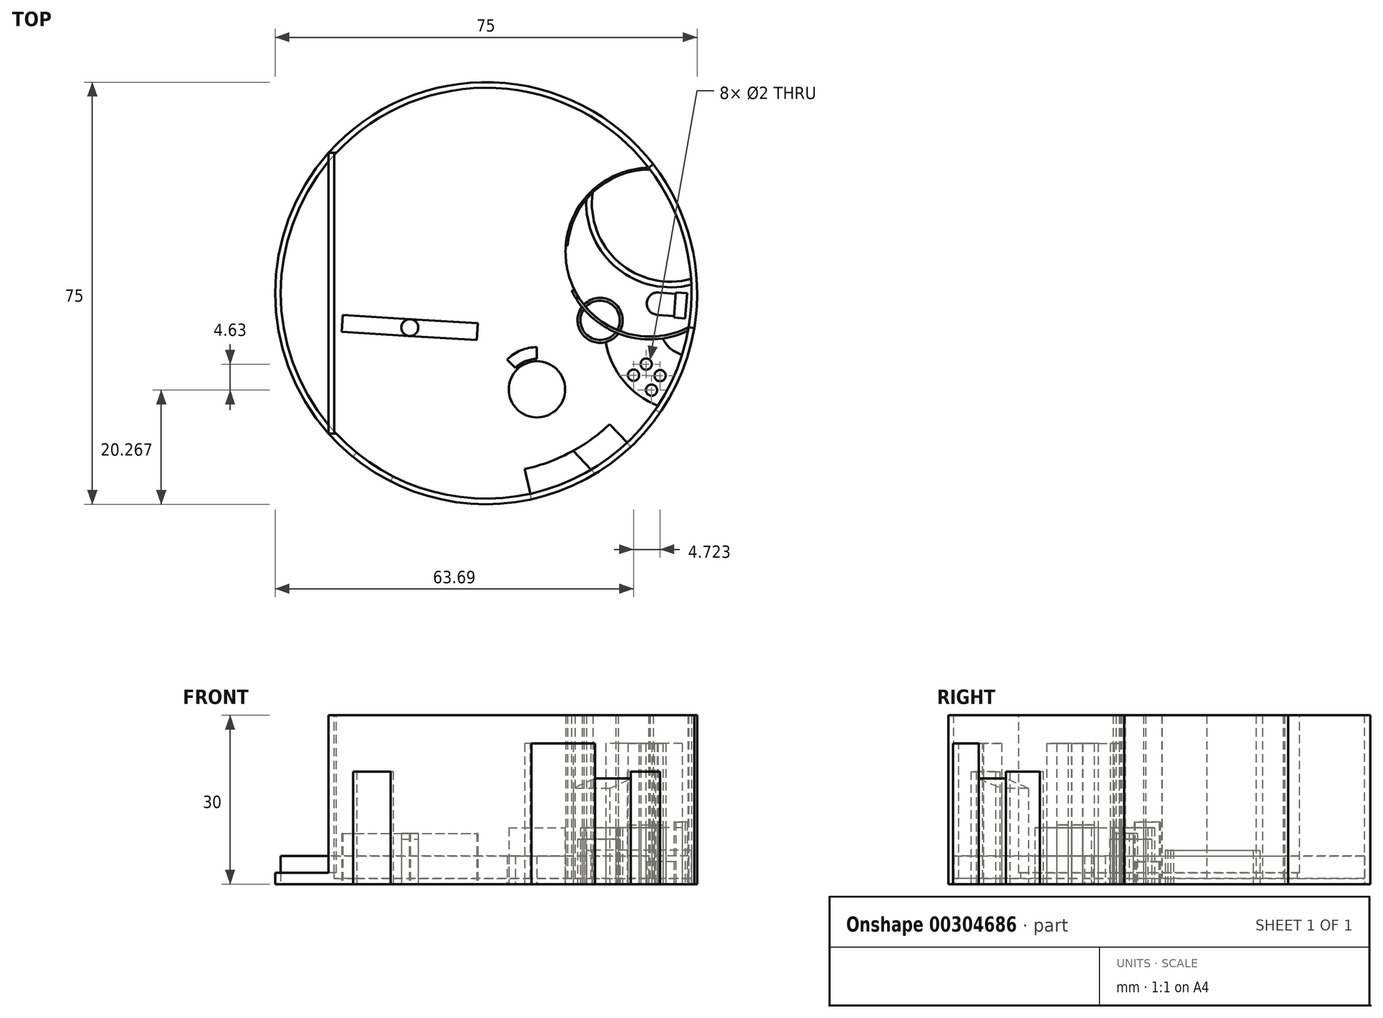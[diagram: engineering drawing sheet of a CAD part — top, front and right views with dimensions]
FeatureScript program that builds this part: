
annotation { "Feature Type Name" : "Feature", "Feature Type Description" : "" }
export const myFeature = defineFeature(function(context is Context, id is Id, definition is map)
    precondition{}
    {
        {
            var Q0;
            Q0=qCreatedBy(makeId("Top.planeOp"),FACE);
            var sketch = newSketch(context, id + "F0", { "sketchPlane" : qUnion([Q0])});
            skCircle(sketch, "E0", {"center": v(0, 0) * mm, "radius": 37.5 * mm});
            skSolve(sketch);
        }
        {
            var Q0;
            Q0=makeQuery(id+"F0.imprint","IMPRINT",FACE,{"disambiguationData":[TD([[makeQuery(id+"F0.imprint","IMPRINT",EDGE,{"derivedFrom":sQuery(id+"F0.wireOp",EDGE,"E0")}),1.0]])]});
            extrude(context, id + "F1", {"entities" : qUnion([Q0]), "oppositeDirection" : true, "depth" : 30 * mm});
        }
        {
            var Q0;
            Q0=qSketchRegion(id+"F0",true);
            var sketch = newSketch(context, id + "F2", { "sketchPlane" : qUnion([Q0])});
            skLineSegment(sketch, "E1", {"start": v(-28, 24.94) * mm, "end": v(-28, -24.94) * mm});
            skSolve(sketch);
        }
        {
            var Q0;
            {var subQ0=sQuery(id+"F2.wireOp",EDGE,"E1");Q0=makeQuery(id+"F2.imprint","IMPRINT",FACE,{"disambiguationData":[TD([[makeQuery(id+"F2.imprint","IMPRINT",EDGE,{"derivedFrom":subQ0}),-1.0]])]});}
            extrude(context, id + "F3", {"entities" : qUnion([Q0]), "operationType" : NewBodyOperationType.REMOVE, "oppositeDirection" : true, "depth" : 28 * mm});
        }
        {
            var Q0;
            {var subQ0=sQuery(id+"F2.wireOp",EDGE,"E1");Q0=makeQuery(id+"F2.imprint","IMPRINT",FACE,{"disambiguationData":[TD([[makeQuery(id+"F2.imprint","IMPRINT",EDGE,{"derivedFrom":subQ0}),1.0]])]});}
            var sketch = newSketch(context, id + "F4", { "sketchPlane" : qUnion([Q0])});
            skCircle(sketch, "E2", {"center": v(0, 0) * mm, "radius": 27 * mm});
            skArc(sketch, "E3", {"start": v(-28, 22.79) * mm, "mid": v(36.1, 0) * mm, "end": v(-28, -22.79) * mm});
            skLineSegment(sketch, "E4", {"start": v(-28, -22.79) * mm, "end": v(-28, 22.79) * mm});
            skSolve(sketch);
        }
        {
            var Q0;
            {var subQ0=sQuery(id+"F2.wireOp",EDGE,"E1");Q0=makeQuery(id+"F2.imprint","IMPRINT",FACE,{"disambiguationData":[TD([[makeQuery(id+"F2.imprint","IMPRINT",EDGE,{"derivedFrom":subQ0}),1.0]])]});}
            var sketch = newSketch(context, id + "F5", { "sketchPlane" : qUnion([Q0])});
            skArc(sketch, "E5", {"start": v(-23.66, -29.1) * mm, "mid": v(-20.43, -31.45) * mm, "end": v(-16.95, -33.45) * mm});
            skSolve(sketch);
        }
        {
            var Q0;
            Q0=makeQuery(id+"F1.opExtrude","CAP_FACE",FACE,{"disambiguationData":[OSD([sQuery(id+"F0.wireOp",EDGE,"E0")])],"isStart":false});
            var sketch = newSketch(context, id + "F6", { "sketchPlane" : qUnion([Q0])});
            skArc(sketch, "E6", {"start": v(-23.66, 29.1) * mm, "mid": v(-20.43, 31.45) * mm, "end": v(-16.95, 33.45) * mm});
            skArc(sketch, "E7", {"start": v(-23.03, 28.32) * mm, "mid": v(-19.88, 30.61) * mm, "end": v(-16.5, 32.56) * mm});
            skLineSegment(sketch, "E8", {"start": v(-23.66, 29.1) * mm, "end": v(-23.03, 28.32) * mm});
            skLineSegment(sketch, "E9", {"start": v(-16.95, 33.45) * mm, "end": v(-16.5, 32.56) * mm});
            skLineSegment(sketch, "E10", {"start": v(0, 0) * mm, "end": v(-23.66, 29.1) * mm, "construction": true});
            skLineSegment(sketch, "E11", {"start": v(-16.95, 33.45) * mm, "end": v(0, 0) * mm, "construction": true});
            skSolve(sketch);
        }
        {
            var Q0;
            Q0=makeQuery(id+"F1.opExtrude","CAP_FACE",FACE,{"disambiguationData":[OSD([sQuery(id+"F0.wireOp",EDGE,"E0")])],"isStart":false});
            var sketch = newSketch(context, id + "F7", { "sketchPlane" : qUnion([Q0])});
            skArc(sketch, "E12", {"start": v(8.05, 36.63) * mm, "mid": v(17.52, 33.15) * mm, "end": v(25.73, 27.28) * mm});
            skArc(sketch, "E13", {"start": v(25.73, 27.28) * mm, "mid": v(28.5, 24.38) * mm, "end": v(30.93, 21.2) * mm});
            skArc(sketch, "E14", {"start": v(30.93, 21.2) * mm, "mid": v(34.78, 14.03) * mm, "end": v(36.98, 6.2) * mm});
            skArc(sketch, "E15", {"start": v(36.98, 6.2) * mm, "mid": v(36.38, -9.1) * mm, "end": v(29.7, -22.9) * mm});
            skLineSegment(sketch, "E16", {"start": v(0, 0) * mm, "end": v(29.7, -22.9) * mm, "construction": true});
            skLineSegment(sketch, "E17", {"start": v(36.98, 6.2) * mm, "end": v(0, 0) * mm, "construction": true});
            skLineSegment(sketch, "E18", {"start": v(30.93, 21.2) * mm, "end": v(0, 0) * mm, "construction": true});
            skLineSegment(sketch, "E19", {"start": v(25.73, 27.28) * mm, "end": v(0, 0) * mm, "construction": true});
            skLineSegment(sketch, "E20", {"start": v(0, 0) * mm, "end": v(8.05, 36.63) * mm, "construction": true});
            skArc(sketch, "E21", {"start": v(6.87, 31.25) * mm, "mid": v(14.95, 28.3) * mm, "end": v(21.96, 23.28) * mm});
            skArc(sketch, "E22", {"start": v(31.56, 5.3) * mm, "mid": v(29.67, 11.98) * mm, "end": v(26.4, 18.1) * mm});
            skLineSegment(sketch, "E23", {"start": v(25.73, 27.28) * mm, "end": v(21.96, 23.28) * mm});
            skLineSegment(sketch, "E24", {"start": v(8.05, 36.63) * mm, "end": v(6.87, 31.25) * mm});
            skLineSegment(sketch, "E25", {"start": v(26.4, 18.1) * mm, "end": v(30.93, 21.2) * mm});
            skLineSegment(sketch, "E26", {"start": v(31.56, 5.3) * mm, "end": v(36.98, 6.2) * mm});
            skArc(sketch, "E27", {"start": v(25.04, 26.55) * mm, "mid": v(27.73, 23.73) * mm, "end": v(30.1, 20.64) * mm});
            skLineSegment(sketch, "E28", {"start": v(30.93, 21.2) * mm, "end": v(30.1, 20.64) * mm});
            skLineSegment(sketch, "E29", {"start": v(25.73, 27.28) * mm, "end": v(25.04, 26.55) * mm});
            skArc(sketch, "E30", {"start": v(36, 6.04) * mm, "mid": v(35.4, -8.86) * mm, "end": v(28.9, -22.29) * mm});
            skLineSegment(sketch, "E31", {"start": v(29.7, -22.9) * mm, "end": v(28.9, -22.29) * mm});
            skLineSegment(sketch, "E32", {"start": v(19.37, 32.1) * mm, "end": v(15.5, 28) * mm});
            skSolve(sketch);
        }
        {
            var Q0;
            Q0=makeQuery(id+"F1.opExtrude","CAP_FACE",FACE,{"disambiguationData":[OSD([sQuery(id+"F0.wireOp",EDGE,"E0")])],"isStart":true});
            shell(context, id + "F8", {"entities" : qUnion([Q0]), "thickness" : 1 * mm});
        }
        {
            var Q0;
            Q0=qSketchRegion(id+"F6",true);
            extrude(context, id + "F9", {"entities" : qUnion([Q0]), "operationType" : NewBodyOperationType.REMOVE, "oppositeDirection" : true, "depth" : 20 * mm});
        }
        {
            var Q0;
            Q0=qSketchRegion(id+"F6",true);
            extrude(context, id + "F10", {"entities" : qUnion([Q0]), "oppositeDirection" : true, "depth" : 20 * mm});
        }
        {
            var Q0;
            Q0=makeQuery(id+"F7.imprint","IMPRINT",FACE,{"disambiguationData":[TD([[makeQuery(id+"F7.imprint","IMPRINT",EDGE,{"derivedFrom":sQuery(id+"F7.wireOp",EDGE,"E12")}),-1.0]])]});
            extrude(context, id + "F11", {"entities" : qUnion([Q0]), "operationType" : NewBodyOperationType.REMOVE, "oppositeDirection" : true, "depth" : 25 * mm});
        }
        {
            var Q0;
            Q0=makeQuery(id+"F7.imprint","IMPRINT",FACE,{"disambiguationData":[TD([[makeQuery(id+"F7.imprint","IMPRINT",EDGE,{"derivedFrom":sQuery(id+"F7.wireOp",EDGE,"E12")}),-1.0]])]});
            extrude(context, id + "F12", {"entities" : qUnion([Q0]), "oppositeDirection" : true, "depth" : 25 * mm});
        }
        {
            var Q0;
            {var subQ0=sQuery(id+"F7.wireOp",EDGE,"E15");Q0=makeQuery(id+"F7.imprint","IMPRINT",FACE,{"disambiguationData":[TD([[makeQuery(id+"F7.imprint","IMPRINT",EDGE,{"derivedFrom":subQ0}),-1.0]])]});}
            extrude(context, id + "F13", {"entities" : qUnion([Q0]), "operationType" : NewBodyOperationType.REMOVE, "oppositeDirection" : true, "depth" : 30 * mm});
        }
        {
            var Q0;
            {var subQ0=sQuery(id+"F7.wireOp",EDGE,"E15");Q0=makeQuery(id+"F7.imprint","IMPRINT",FACE,{"disambiguationData":[TD([[makeQuery(id+"F7.imprint","IMPRINT",EDGE,{"derivedFrom":subQ0}),-1.0]])]});}
            extrude(context, id + "F14", {"entities" : qUnion([Q0]), "oppositeDirection" : true, "depth" : 30 * mm});
        }
        {
            var Q0;
            Q0=makeQuery(id+"F7.imprint","IMPRINT",FACE,{"disambiguationData":[TD([[makeQuery(id+"F7.imprint","IMPRINT",EDGE,{"derivedFrom":sQuery(id+"F7.wireOp",EDGE,"E13")}),-1.0]])]});
            extrude(context, id + "F15", {"entities" : qUnion([Q0]), "operationType" : NewBodyOperationType.REMOVE, "oppositeDirection" : true, "depth" : 20 * mm});
        }
        {
            var Q0;
            Q0=makeQuery(id+"F7.imprint","IMPRINT",FACE,{"disambiguationData":[TD([[makeQuery(id+"F7.imprint","IMPRINT",EDGE,{"derivedFrom":sQuery(id+"F7.wireOp",EDGE,"E13")}),-1.0]])]});
            extrude(context, id + "F16", {"entities" : qUnion([Q0]), "oppositeDirection" : true, "depth" : 20 * mm});
        }
        {
            var Q0;
            Q0=makeQuery(id+"F3.boolean.opBoolean","COPY",FACE,{"derivedFrom":makeQuery(id+"F3.opExtrude","SWEPT_FACE",FACE,{"disambiguationData":[OSD([sQuery(id+"F2.wireOp",EDGE,"E1")])]})});
            var sketch = newSketch(context, id + "F17", { "sketchPlane" : qUnion([Q0])});
            skLineSegment(sketch, "E33", {"start": v(24.94, -28) * mm, "end": v(24.94, 0) * mm});
            skLineSegment(sketch, "E34", {"start": v(24.94, 0) * mm, "end": v(-24.94, 0) * mm});
            skLineSegment(sketch, "E35", {"start": v(-24.94, 0) * mm, "end": v(-24.94, -28) * mm});
            skLineSegment(sketch, "E36", {"start": v(-24.94, -28) * mm, "end": v(24.94, -28) * mm});
            skSolve(sketch);
        }
        {
            var Q0;
            Q0=makeQuery(id+"F17.imprint","IMPRINT",FACE,{"disambiguationData":[TD([[makeQuery(id+"F17.imprint","IMPRINT",EDGE,{"derivedFrom":sQuery(id+"F17.wireOp",EDGE,"E33")}),1.0]])]});
            extrude(context, id + "F18", {"entities" : qUnion([Q0]), "operationType" : NewBodyOperationType.REMOVE, "endBound" : BoundingType.UP_TO_NEXT, "oppositeDirection" : true, "depth" : 25 * mm});
        }
        {
            var Q0;
            Q0=makeQuery(id+"F17.imprint","IMPRINT",FACE,{"disambiguationData":[TD([[makeQuery(id+"F17.imprint","IMPRINT",EDGE,{"derivedFrom":sQuery(id+"F17.wireOp",EDGE,"E33")}),1.0]])]});
            extrude(context, id + "F19", {"entities" : qUnion([Q0]), "oppositeDirection" : true, "depth" : 1 * mm});
        }
        {
            var Q0;
            Q0=makeQuery(id+"F6.imprint","IMPRINT",FACE,{"disambiguationData":[TD([[makeQuery(id+"F6.imprint","IMPRINT",EDGE,{"derivedFrom":sQuery(id+"F6.wireOp",EDGE,"E7")}),-1.0]])]});
            var sketch = newSketch(context, id + "F20", { "sketchPlane" : qUnion([Q0])});
            skCircle(sketch, "E37", {"center": v(-1.82, -23.91) * mm, "radius": 12.12 * mm});
            skCircle(sketch, "E38", {"center": v(-13.57, 6.12) * mm, "radius": 12.12 * mm});
            skArc(sketch, "E39", {"start": v(28.9, -22.29) * mm, "mid": v(35.4, -8.86) * mm, "end": v(36, 6.04) * mm});
            skArc(sketch, "E40", {"start": v(28.9, -22.29) * mm, "mid": v(14.56, -3.65) * mm, "end": v(36, 6.04) * mm});
            skArc(sketch, "E41", {"start": v(28.9, -22.29) * mm, "mid": v(-35.4, 8.86) * mm, "end": v(36, 6.04) * mm});
            skLineSegment(sketch, "E42", {"start": v(15.9, -14.39) * mm, "end": v(8.85, -18.17) * mm});
            skLineSegment(sketch, "E43", {"start": v(-6.24, -12.62) * mm, "end": v(-9.15, -5.17) * mm});
            skLineSegment(sketch, "E44", {"start": v(-13.57, 6.12) * mm, "end": v(-1.82, -23.91) * mm, "construction": true});
            skLineSegment(sketch, "E45", {"start": v(-1.82, -23.91) * mm, "end": v(29.11, -7.29) * mm, "construction": true});
            skLineSegment(sketch, "E46", {"start": v(-2.66, 11.41) * mm, "end": v(4.53, 14.9) * mm});
            skLineSegment(sketch, "E47", {"start": v(-13.57, 6.12) * mm, "end": v(9.03, 17.09) * mm, "construction": true});
            skPoint(sketch, "E48.middle", {"position": v(9.03, 17.09) * mm});
            skArc(sketch, "E49", {"start": v(9.03, 11.68) * mm, "mid": v(6.96, 12.1) * mm, "end": v(5.2, 13.26) * mm});
            skArc(sketch, "E50", {"start": v(3.73, 11.79) * mm, "mid": v(6.16, 10.16) * mm, "end": v(9.03, 9.59) * mm});
            skArc(sketch, "E51", {"start": v(14.33, 11.79) * mm, "mid": v(15.96, 14.22) * mm, "end": v(16.53, 17.09) * mm});
            skArc(sketch, "E52", {"start": v(14.44, 17.09) * mm, "mid": v(14.03, 15.02) * mm, "end": v(12.86, 13.26) * mm});
            skArc(sketch, "E53", {"start": v(12.86, 20.91) * mm, "mid": v(11.1, 22.09) * mm, "end": v(9.03, 22.5) * mm});
            skArc(sketch, "E54", {"start": v(14.33, 22.4) * mm, "mid": v(11.9, 24.02) * mm, "end": v(9.03, 24.59) * mm});
            skArc(sketch, "E55", {"start": v(5.2, 20.91) * mm, "mid": v(4.03, 19.16) * mm, "end": v(3.62, 17.09) * mm});
            skArc(sketch, "E56", {"start": v(3.73, 22.4) * mm, "mid": v(2.1, 19.96) * mm, "end": v(1.53, 17.09) * mm});
            skLineSegment(sketch, "E57", {"start": v(16.53, 17.09) * mm, "end": v(14.44, 17.09) * mm});
            skLineSegment(sketch, "E58", {"start": v(12.86, 13.26) * mm, "end": v(14.33, 11.79) * mm});
            skLineSegment(sketch, "E59", {"start": v(9.03, 11.68) * mm, "end": v(9.03, 9.59) * mm});
            skLineSegment(sketch, "E60", {"start": v(5.2, 13.26) * mm, "end": v(3.73, 11.79) * mm});
            skLineSegment(sketch, "E61", {"start": v(3.62, 17.09) * mm, "end": v(1.53, 17.09) * mm});
            skLineSegment(sketch, "E62", {"start": v(5.2, 20.91) * mm, "end": v(3.73, 22.4) * mm});
            skLineSegment(sketch, "E63", {"start": v(9.03, 22.5) * mm, "end": v(9.03, 24.59) * mm});
            skLineSegment(sketch, "E64", {"start": v(12.86, 20.91) * mm, "end": v(14.33, 22.4) * mm});
            skCircle(sketch, "E65", {"center": v(9.03, 17.09) * mm, "radius": 5 * mm});
            skLineSegment(sketch, "E66", {"start": v(9.03, 17.09) * mm, "end": v(6.87, 31.25) * mm, "construction": true});
            skLineSegment(sketch, "E67", {"start": v(9.03, 17.09) * mm, "end": v(21.96, 23.28) * mm, "construction": true});
            skSolve(sketch);
        }
        {
            var Q0;
            Q0=makeQuery(id+"F6.imprint","IMPRINT",FACE,{"disambiguationData":[TD([[makeQuery(id+"F6.imprint","IMPRINT",EDGE,{"derivedFrom":sQuery(id+"F6.wireOp",EDGE,"E7")}),-1.0]])]});
            var sketch = newSketch(context, id + "F21", { "sketchPlane" : qUnion([Q0])});
            skCircle(sketch, "E68", {"center": v(-13.57, 6.12) * mm, "radius": 1.5 * mm});
            skLineSegment(sketch, "E69", {"start": v(-25.66, 6.88) * mm, "end": v(-1.65, 8.34) * mm});
            skLineSegment(sketch, "E70", {"start": v(-25.48, 3.89) * mm, "end": v(-1.47, 5.35) * mm});
            skArc(sketch, "E71", {"start": v(30.53, 20) * mm, "mid": v(24.4, 15.56) * mm, "end": v(21.23, 8.7) * mm});
            skLineSegment(sketch, "E72", {"start": v(35.36, 4.48) * mm, "end": v(35.7, 0) * mm});
            skLineSegment(sketch, "E73", {"start": v(35.7, 0) * mm, "end": v(33.71, -0.16) * mm});
            skLineSegment(sketch, "E74", {"start": v(33.71, -0.16) * mm, "end": v(33.37, 4.33) * mm});
            skLineSegment(sketch, "E75", {"start": v(33.37, 4.33) * mm, "end": v(35.36, 4.48) * mm});
            skLineSegment(sketch, "E76", {"start": v(33.7, 0.1) * mm, "end": v(30.7, -0.14) * mm});
            skLineSegment(sketch, "E77", {"start": v(33.38, 4.08) * mm, "end": v(30.4, 3.85) * mm});
            skArc(sketch, "E78", {"start": v(30.4, 3.85) * mm, "mid": v(28.55, 1.7) * mm, "end": v(30.7, -0.14) * mm});
            skArc(sketch, "E79", {"start": v(17.83, -17.17) * mm, "mid": v(23.13, -4.56) * mm, "end": v(36.47, -1.5) * mm});
            skArc(sketch, "E80", {"start": v(36, 6.04) * mm, "mid": v(14.56, -3.65) * mm, "end": v(28.9, -22.29) * mm, "construction": true});
            skArc(sketch, "E81", {"start": v(28.52, -22.78) * mm, "mid": v(14.08, -3.52) * mm, "end": v(35.89, 6.65) * mm, "construction": true});
            skArc(sketch, "E82", {"start": v(36, 6.04) * mm, "mid": v(24.55, 7) * mm, "end": v(15.77, -0.43) * mm});
            skArc(sketch, "E83", {"start": v(35.89, 6.65) * mm, "mid": v(24.07, 7.37) * mm, "end": v(15.2, -0.47) * mm});
            skArc(sketch, "E84", {"start": v(28.9, -22.29) * mm, "mid": v(18.85, -18.23) * mm, "end": v(14.16, -8.45) * mm});
            skArc(sketch, "E85", {"start": v(28.52, -22.78) * mm, "mid": v(18.37, -18.46) * mm, "end": v(13.66, -8.49) * mm});
            skLineSegment(sketch, "E86", {"start": v(15.2, -0.47) * mm, "end": v(15.77, -0.43) * mm});
            skArc(sketch, "E87", {"start": v(14.46, -8.43) * mm, "mid": v(19.13, -18.08) * mm, "end": v(29.11, -21.99) * mm});
            skArc(sketch, "E88", {"start": v(28.29, -23.07) * mm, "mid": v(18.08, -18.6) * mm, "end": v(13.36, -8.51) * mm});
            skLineSegment(sketch, "E89", {"start": v(13.36, -8.51) * mm, "end": v(13.66, -8.49) * mm});
            skLineSegment(sketch, "E90", {"start": v(14.16, -8.45) * mm, "end": v(14.46, -8.43) * mm});
            skLineSegment(sketch, "E91", {"start": v(28.9, -22.29) * mm, "end": v(29.11, -21.99) * mm});
            skLineSegment(sketch, "E92", {"start": v(28.29, -23.07) * mm, "end": v(28.52, -22.78) * mm});
            skCircle(sketch, "E93", {"center": v(26.2, 14.57) * mm, "radius": 1 * mm});
            skCircle(sketch, "E94", {"center": v(29.39, 17.23) * mm, "radius": 1 * mm});
            skCircle(sketch, "E95", {"center": v(30.91, 14.65) * mm, "radius": 1 * mm});
            skCircle(sketch, "E96", {"center": v(28.45, 12.6) * mm, "radius": 1 * mm});
            skLineSegment(sketch, "E97", {"start": v(-1.47, 5.35) * mm, "end": v(-1.65, 8.34) * mm});
            skLineSegment(sketch, "E98", {"start": v(-25.48, 3.89) * mm, "end": v(-25.66, 6.88) * mm});
            skArc(sketch, "E99", {"start": v(17.7, 2.43) * mm, "mid": v(22.32, 2) * mm, "end": v(23.3, 6.54) * mm});
            skArc(sketch, "E100", {"start": v(23.77, 6.73) * mm, "mid": v(22.62, 1.59) * mm, "end": v(17.37, 2.04) * mm});
            skArc(sketch, "E101", {"start": v(17.37, 2.83) * mm, "mid": v(18.19, 7.64) * mm, "end": v(23.02, 6.96) * mm});
            skArc(sketch, "E102", {"start": v(17.04, 2.43) * mm, "mid": v(17.9, 8.04) * mm, "end": v(23.5, 7.16) * mm});
            skLineSegment(sketch, "E103", {"start": v(17.04, 2.43) * mm, "end": v(17.37, 2.83) * mm});
            skLineSegment(sketch, "E104", {"start": v(17.37, 2.04) * mm, "end": v(17.7, 2.43) * mm});
            skLineSegment(sketch, "E105", {"start": v(23.3, 6.54) * mm, "end": v(23.77, 6.73) * mm});
            skLineSegment(sketch, "E106", {"start": v(23.02, 6.96) * mm, "end": v(23.5, 7.16) * mm});
            skLineSegment(sketch, "E107", {"start": v(36, 6.04) * mm, "end": v(35.89, 6.65) * mm});
            skArc(sketch, "E108", {"start": v(30.53, 20) * mm, "mid": v(33.87, 13.6) * mm, "end": v(35.89, 6.65) * mm});
            skArc(sketch, "E109", {"start": v(36.41, -2.52) * mm, "mid": v(23.38, -5.68) * mm, "end": v(18.98, -18.34) * mm});
            skLineSegment(sketch, "E110", {"start": v(36.47, -1.5) * mm, "end": v(36.41, -2.52) * mm});
            skLineSegment(sketch, "E111", {"start": v(17.83, -17.17) * mm, "end": v(18.98, -18.34) * mm});
            skLineSegment(sketch, "E112", {"start": v(36, 6.04) * mm, "end": v(20.25, 4.82) * mm, "construction": true});
            skLineSegment(sketch, "E113", {"start": v(36, 6.04) * mm, "end": v(24.68, 15.88) * mm, "construction": true});
            skLineSegment(sketch, "E114", {"start": v(36, 6.04) * mm, "end": v(28.37, 18.95) * mm, "construction": true});
            skArc(sketch, "E115", {"start": v(31.6, 18.27) * mm, "mid": v(25.84, 14.15) * mm, "end": v(23.1, 7.63) * mm, "construction": true});
            skArc(sketch, "E116", {"start": v(33, 15.58) * mm, "mid": v(28.54, 12.7) * mm, "end": v(26.18, 7.93) * mm, "construction": true});
            skArc(sketch, "E117", {"start": v(31.41, 8.04) * mm, "mid": v(32.79, 9.87) * mm, "end": v(34.83, 10.9) * mm});
            skSolve(sketch);
        }
        {
            var Q0;
            {var subQ0=sQuery(id+"F20.wireOp",EDGE,"E38");var subQ1=makeQuery(id+"F20.imprint","IMPRINT",VERTEX,{"disambiguationData":[OD(0.0)],"derivedFrom":subQ0});Q0=makeQuery(id+"F20.imprint","IMPRINT",FACE,{"disambiguationData":[TD([[makeQuery(id+"F20.imprint","IMPRINT",EDGE,{"disambiguationData":[TD([[subQ1,1.0]])],"derivedFrom":subQ0}),1.0]])]});}
            var Q1;
            {var subQ0=sQuery(id+"F20.wireOp",EDGE,"E37");var subQ1=makeQuery(id+"F20.imprint","IMPRINT",VERTEX,{"disambiguationData":[OD(0.0)],"derivedFrom":subQ0});Q1=makeQuery(id+"F20.imprint","IMPRINT",FACE,{"disambiguationData":[TD([[makeQuery(id+"F20.imprint","IMPRINT",EDGE,{"disambiguationData":[TD([[subQ1,-1.0]])],"derivedFrom":subQ0}),1.0]])]});}
            var Q2;
            Q2=makeQuery(id+"F20.imprint","IMPRINT",FACE,{"disambiguationData":[TD([[makeQuery(id+"F20.imprint","IMPRINT",EDGE,{"derivedFrom":sQuery(id+"F20.wireOp",EDGE,"E55")}),-1.0]])]});
            var Q3;
            Q3=makeQuery(id+"F20.imprint","IMPRINT",FACE,{"disambiguationData":[TD([[makeQuery(id+"F20.imprint","IMPRINT",EDGE,{"derivedFrom":sQuery(id+"F20.wireOp",EDGE,"E49")}),1.0]])]});
            var Q4;
            Q4=makeQuery(id+"F20.imprint","IMPRINT",FACE,{"disambiguationData":[TD([[makeQuery(id+"F20.imprint","IMPRINT",EDGE,{"derivedFrom":sQuery(id+"F20.wireOp",EDGE,"E51")}),1.0]])]});
            var Q5;
            Q5=makeQuery(id+"F20.imprint","IMPRINT",FACE,{"disambiguationData":[TD([[makeQuery(id+"F20.imprint","IMPRINT",EDGE,{"derivedFrom":sQuery(id+"F20.wireOp",EDGE,"E53")}),-1.0]])]});
            extrude(context, id + "F22", {"entities" : qUnion([Q0, Q1, Q2, Q3, Q4, Q5]), "oppositeDirection" : true, "depth" : 5 * mm});
        }
        {
            var Q0;
            Q0=makeQuery(id+"F20.imprint","IMPRINT",FACE,{"disambiguationData":[TD([[makeQuery(id+"F20.imprint","IMPRINT",EDGE,{"derivedFrom":sQuery(id+"F20.wireOp",EDGE,"E65")}),1.0]])]});
            extrude(context, id + "F23", {"entities" : qUnion([Q0]), "oppositeDirection" : true, "depth" : 10 * mm});
        }
        {
            var Q0;
            {var subQ5=sQuery(id+"F21.wireOp",EDGE,"E97");Q0=makeQuery(id+"F21.imprint","IMPRINT",FACE,{"disambiguationData":[TD([[makeQuery(id+"F21.imprint","IMPRINT",EDGE,{"derivedFrom":subQ5}),1.0]])]});}
            var Q1;
            {var subQ5=sQuery(id+"F21.wireOp",EDGE,"E98");Q1=makeQuery(id+"F21.imprint","IMPRINT",FACE,{"disambiguationData":[TD([[makeQuery(id+"F21.imprint","IMPRINT",EDGE,{"derivedFrom":subQ5}),-1.0]])]});}
            extrude(context, id + "F24", {"entities" : qUnion([Q0, Q1]), "oppositeDirection" : true, "depth" : 9 * mm});
        }
        {
            var Q0;
            {var subQ0=sQuery(id+"F21.wireOp",EDGE,"E68");var subQ1=makeQuery(id+"F21.imprint","INTERSECT",VERTEX,{"derivedFrom":[subQ0,sQuery(id+"F21.wireOp",EDGE,"E69")]});Q0=makeQuery(id+"F21.imprint","IMPRINT",FACE,{"disambiguationData":[TD([[makeQuery(id+"F21.imprint","IMPRINT",EDGE,{"disambiguationData":[TD([[subQ1,-1.0]])],"derivedFrom":subQ0}),1.0]])]});}
            extrude(context, id + "F25", {"entities" : qUnion([Q0]), "oppositeDirection" : true, "depth" : 8 * mm});
        }
        {
            var Q0;
            {var subQ0=sQuery(id+"F21.wireOp",EDGE,"E86");Q0=makeQuery(id+"F21.imprint","IMPRINT",FACE,{"disambiguationData":[TD([[makeQuery(id+"F21.imprint","IMPRINT",EDGE,{"derivedFrom":subQ0}),1.0]])]});}
            var Q1;
            {var subQ0=sQuery(id+"F21.wireOp",EDGE,"E91");Q1=makeQuery(id+"F21.imprint","IMPRINT",FACE,{"disambiguationData":[TD([[makeQuery(id+"F21.imprint","IMPRINT",EDGE,{"derivedFrom":subQ0}),1.0]])]});}
            var Q2;
            Q2=makeQuery(id+"F21.imprint","IMPRINT",FACE,{"disambiguationData":[TD([[makeQuery(id+"F21.imprint","IMPRINT",EDGE,{"derivedFrom":sQuery(id+"F21.wireOp",EDGE,"E85")}),1.0]])]});
            var Q3;
            {var subQ5=sQuery(id+"F21.wireOp",EDGE,"E90");Q3=makeQuery(id+"F21.imprint","IMPRINT",FACE,{"disambiguationData":[TD([[makeQuery(id+"F21.imprint","IMPRINT",EDGE,{"derivedFrom":subQ5}),-1.0]])]});}
            var Q4;
            {var subQ0=sQuery(id+"F21.wireOp",EDGE,"E111");Q4=makeQuery(id+"F21.imprint","IMPRINT",FACE,{"disambiguationData":[TD([[makeQuery(id+"F21.imprint","IMPRINT",EDGE,{"derivedFrom":subQ0}),1.0]])]});}
            extrude(context, id + "F26", {"entities" : qUnion([Q0, Q1, Q2, Q3, Q4]), "oppositeDirection" : true, "depth" : 30 * mm});
        }
        {
            var Q0;
            {var subQ0=sQuery(id+"F21.wireOp",EDGE,"E110");Q0=makeQuery(id+"F21.imprint","IMPRINT",FACE,{"disambiguationData":[TD([[makeQuery(id+"F21.imprint","IMPRINT",EDGE,{"derivedFrom":subQ0}),-1.0]])]});}
            extrude(context, id + "F27", {"entities" : qUnion([Q0]), "oppositeDirection" : true, "depth" : 6 * mm});
        }
        {
            var Q0;
            {var subQ0=sQuery(id+"F21.wireOp",EDGE,"E76");Q0=makeQuery(id+"F21.imprint","IMPRINT",FACE,{"disambiguationData":[TD([[makeQuery(id+"F21.imprint","IMPRINT",EDGE,{"derivedFrom":subQ0}),-1.0]])]});}
            extrude(context, id + "F28", {"entities" : qUnion([Q0]), "oppositeDirection" : true, "depth" : 4 * mm});
        }
        {
            var Q0;
            Q0=makeQuery(id+"F21.imprint","IMPRINT",FACE,{"disambiguationData":[TD([[makeQuery(id+"F21.imprint","IMPRINT",EDGE,{"derivedFrom":sQuery(id+"F21.wireOp",EDGE,"E96")}),1.0]])]});
            var Q1;
            Q1=makeQuery(id+"F21.imprint","IMPRINT",FACE,{"disambiguationData":[TD([[makeQuery(id+"F21.imprint","IMPRINT",EDGE,{"derivedFrom":sQuery(id+"F21.wireOp",EDGE,"E94")}),1.0]])]});
            var Q2;
            Q2=makeQuery(id+"F21.imprint","IMPRINT",FACE,{"disambiguationData":[TD([[makeQuery(id+"F21.imprint","IMPRINT",EDGE,{"derivedFrom":sQuery(id+"F21.wireOp",EDGE,"E93")}),1.0]])]});
            var Q3;
            Q3=makeQuery(id+"F21.imprint","IMPRINT",FACE,{"disambiguationData":[TD([[makeQuery(id+"F21.imprint","IMPRINT",EDGE,{"derivedFrom":sQuery(id+"F21.wireOp",EDGE,"E95")}),1.0]])]});
            extrude(context, id + "F29", {"entities" : qUnion([Q0, Q1, Q2, Q3]), "oppositeDirection" : true, "depth" : 10.5 * mm});
        }
        {
            var Q0;
            Q0=makeQuery(id+"F21.imprint","IMPRINT",FACE,{"disambiguationData":[TD([[makeQuery(id+"F21.imprint","IMPRINT",EDGE,{"derivedFrom":sQuery(id+"F21.wireOp",EDGE,"E72")}),-1.0]])]});
            extrude(context, id + "F30", {"entities" : qUnion([Q0]), "oppositeDirection" : true, "depth" : 11 * mm});
        }
        {
            var Q0;
            {var subQ5=sQuery(id+"F21.wireOp",EDGE,"E101");Q0=makeQuery(id+"F21.imprint","IMPRINT",FACE,{"disambiguationData":[TD([[makeQuery(id+"F21.imprint","IMPRINT",EDGE,{"derivedFrom":subQ5}),1.0]])]});}
            var Q1;
            Q1=makeQuery(id+"F21.imprint","IMPRINT",FACE,{"disambiguationData":[TD([[makeQuery(id+"F21.imprint","IMPRINT",EDGE,{"derivedFrom":sQuery(id+"F21.wireOp",EDGE,"E99")}),-1.0]])]});
            var Q2;
            {var subQ4=sQuery(id+"F21.wireOp",EDGE,"E71");Q2=makeQuery(id+"F21.imprint","IMPRINT",FACE,{"disambiguationData":[TD([[makeQuery(id+"F21.imprint","IMPRINT",EDGE,{"derivedFrom":subQ4}),1.0]])]});}
            extrude(context, id + "F31", {"entities" : qUnion([Q0, Q1, Q2]), "oppositeDirection" : true, "depth" : 10 * mm});
        }
        {
            var Q0;
            {var subQ0=sQuery(id+"F21.wireOp",EDGE,"E101");Q0=makeQuery(id+"F21.imprint","IMPRINT",FACE,{"disambiguationData":[TD([[makeQuery(id+"F21.imprint","IMPRINT",EDGE,{"derivedFrom":subQ0}),-1.0]])]});}
            var Q1;
            {var subQ0=sQuery(id+"F21.wireOp",EDGE,"E99");Q1=makeQuery(id+"F21.imprint","IMPRINT",FACE,{"disambiguationData":[TD([[makeQuery(id+"F21.imprint","IMPRINT",EDGE,{"derivedFrom":subQ0}),1.0]])]});}
            extrude(context, id + "F32", {"entities" : qUnion([Q0, Q1]), "oppositeDirection" : true, "depth" : 8 * mm});
        }
        {
            var Q0;
            {var subQ3=sQuery(id+"F21.wireOp",EDGE,"E117");Q0=makeQuery(id+"F21.imprint","IMPRINT",FACE,{"disambiguationData":[TD([[makeQuery(id+"F21.imprint","IMPRINT",EDGE,{"derivedFrom":subQ3}),-1.0]])]});}
            extrude(context, id + "F33", {"entities" : qUnion([Q0]), "oppositeDirection" : true, "depth" : 25 * mm});
        }
        {
            var Q0;
            {var subQ1=sQuery(id+"F7.wireOp",EDGE,"E23");Q0=makeQuery(id+"F7.imprint","IMPRINT",FACE,{"disambiguationData":[TD([[makeQuery(id+"F7.imprint","IMPRINT",EDGE,{"derivedFrom":subQ1}),-1.0]])]});}
            extrude(context, id + "F34", {"entities" : qUnion([Q0]), "oppositeDirection" : true, "depth" : 25 * mm});
        }
        {
            var Q0;
            Q0=makeQuery(id+"F34.opExtrude","CAP_EDGE",EDGE,{"disambiguationData":[OSD([sQuery(id+"F7.wireOp",EDGE,"E21")])],"isStart":false});
            chamfer(context, id + "F35", {"entities" : qUnion([Q0]), "chamferType" : ChamferType.TWO_OFFSETS, "width1" : 8 * mm, "oppositeDirection" : true, "width2" : 25 * mm, "tangentPropagation" : true});
        }
    });
